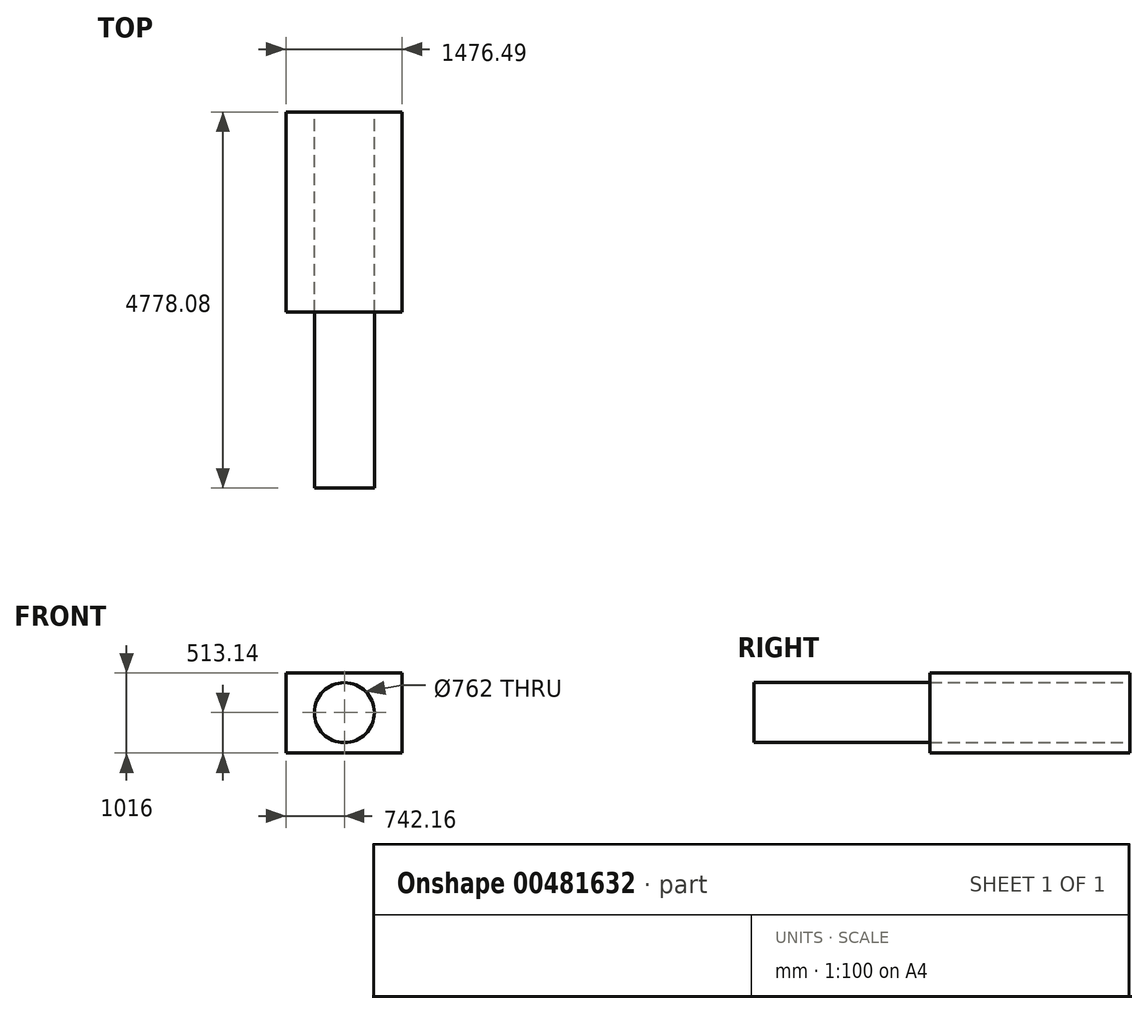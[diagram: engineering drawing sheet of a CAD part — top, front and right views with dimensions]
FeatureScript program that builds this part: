
annotation { "Feature Type Name" : "Feature", "Feature Type Description" : "" }
export const myFeature = defineFeature(function(context is Context, id is Id, definition is map)
    precondition{}
    {
        {
            var Q0;
            Q0=qCreatedBy(makeId("Front.planeOp"),FACE);
            var sketch = newSketch(context, id + "F0", { "sketchPlane" : qUnion([Q0])});
            skLineSegment(sketch, "E0.bottom", {"start": v(-742.16, 502.86) * mm, "end": v(734.33, 502.86) * mm});
            skLineSegment(sketch, "E0.top", {"start": v(-742.16, -513.14) * mm, "end": v(734.33, -513.14) * mm});
            skLineSegment(sketch, "E0.left", {"start": v(-742.16, 502.86) * mm, "end": v(-742.16, -513.14) * mm});
            skLineSegment(sketch, "E0.right", {"start": v(734.33, 502.86) * mm, "end": v(734.33, -513.14) * mm});
            skCircle(sketch, "E1", {"center": v(0, 0) * mm, "radius": 381 * mm});
            skSolve(sketch);
        }
        {
            var Q0;
            Q0 = qSketchRegion(id + "F0", true);
            extrude(context, id + "F1", {"entities" : qUnion([Q0]), "depth" : 2540 * mm});
        }
        {
            var Q0;
            Q0=makeQuery(id+"F1.opExtrude","CAP_FACE",FACE,{"disambiguationData":[OSD([sQuery(id+"F0.wireOp",EDGE,"E0.bottom"),sQuery(id+"F0.wireOp",EDGE,"E0.top"),sQuery(id+"F0.wireOp",EDGE,"E0.left"),sQuery(id+"F0.wireOp",EDGE,"E0.right"),sQuery(id+"F0.wireOp",EDGE,"E1")])],"isStart":false});
            var sketch = newSketch(context, id + "F2", { "sketchPlane" : qUnion([Q0])});
            skCircle(sketch, "E2", {"center": v(0, 0) * mm, "radius": 381 * mm});
            skSolve(sketch);
        }
        {
            var Q0;
            Q0 = qSketchRegion(id + "F2", true);
            extrude(context, id + "F3", {"entities" : qUnion([Q0]), "depth" : 2238.08 * mm});
        }
    });
